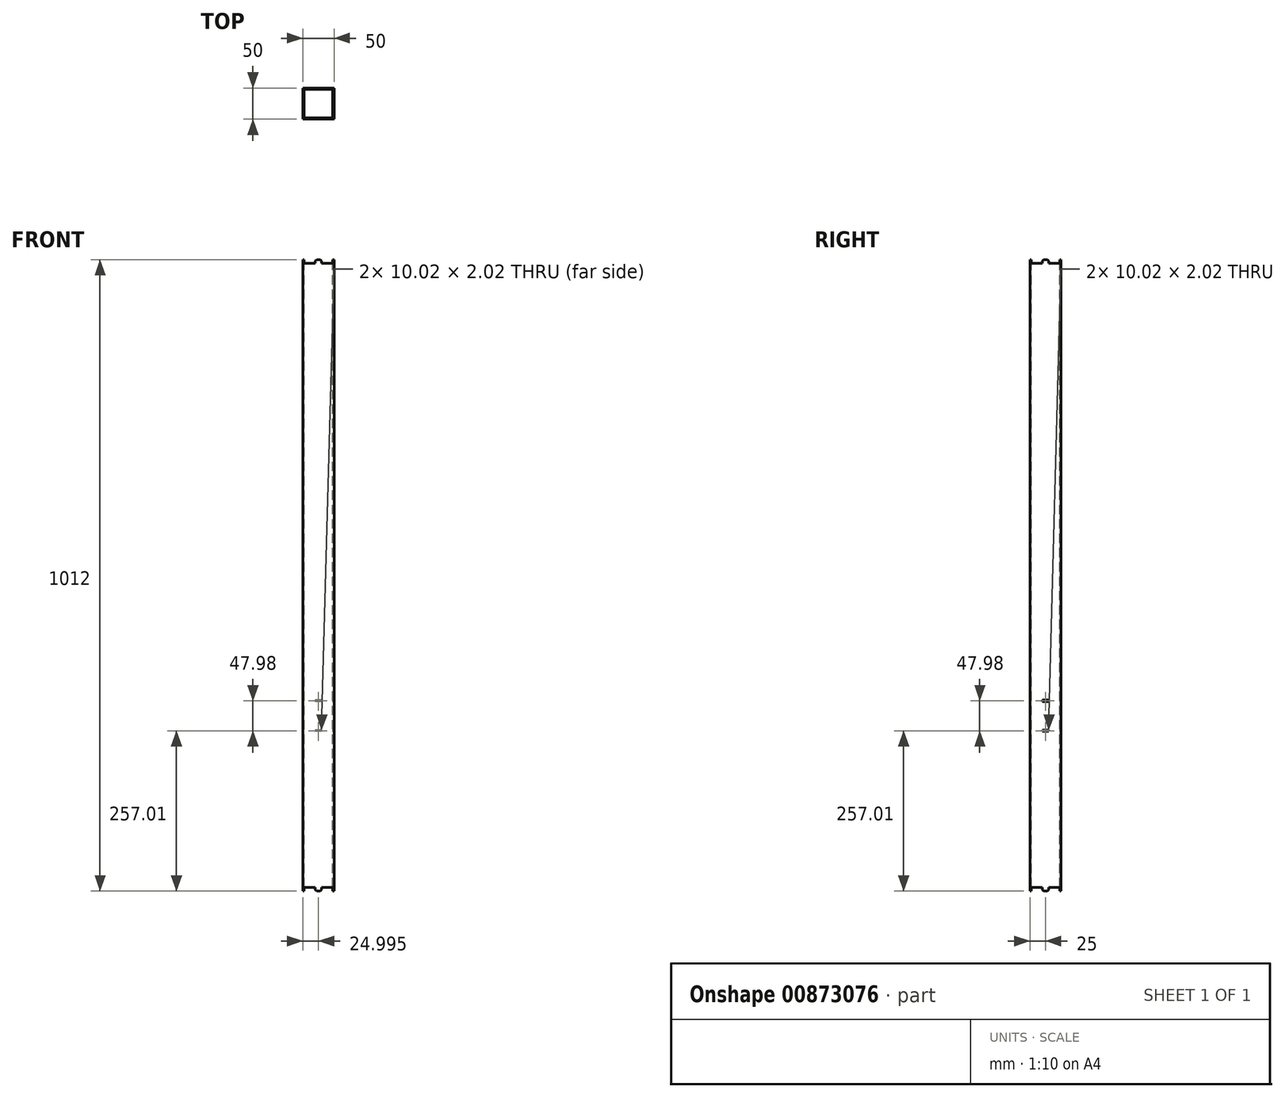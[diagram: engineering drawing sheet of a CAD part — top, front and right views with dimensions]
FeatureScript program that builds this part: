
annotation { "Feature Type Name" : "Feature", "Feature Type Description" : "" }
export const myFeature = defineFeature(function(context is Context, id is Id, definition is map)
    precondition{}
    {
        {
            var Q0;
            Q0=qCreatedBy(makeId("Front.planeOp"),FACE);
            var sketch = newSketch(context, id + "F0", { "sketchPlane" : qUnion([Q0])});
            skLineSegment(sketch, "E0.bottom", {"start": v(-56.86, 862.27) * mm, "end": v(-36.86, 862.27) * mm});
            skLineSegment(sketch, "E0.top", {"start": v(-56.86, -137.73) * mm, "end": v(-36.86, -137.73) * mm});
            skLineSegment(sketch, "E0.left", {"start": v(-56.86, 862.27) * mm, "end": v(-56.86, -137.73) * mm});
            skLineSegment(sketch, "E0.right", {"start": v(-6.86, 862.27) * mm, "end": v(-6.86, -137.73) * mm});
            skLineSegment(sketch, "E1", {"start": v(-36.86, -137.73) * mm, "end": v(-36.86, -141.73) * mm});
            skLineSegment(sketch, "E2", {"start": v(-36.86, -141.73) * mm, "end": v(-34.86, -143.73) * mm});
            skLineSegment(sketch, "E3", {"start": v(-34.86, -143.73) * mm, "end": v(-28.86, -143.73) * mm});
            skLineSegment(sketch, "E4", {"start": v(-28.86, -143.73) * mm, "end": v(-26.86, -141.73) * mm});
            skLineSegment(sketch, "E5", {"start": v(-26.86, -141.73) * mm, "end": v(-26.86, -137.73) * mm});
            skLineSegment(sketch, "E6.trimOffspring", {"start": v(-26.86, -137.73) * mm, "end": v(-6.86, -137.73) * mm});
            skLineSegment(sketch, "E7", {"start": v(-36.86, 862.27) * mm, "end": v(-36.86, 866.27) * mm});
            skLineSegment(sketch, "E8", {"start": v(-36.86, 866.27) * mm, "end": v(-34.86, 868.27) * mm});
            skLineSegment(sketch, "E9", {"start": v(-34.86, 868.27) * mm, "end": v(-28.86, 868.27) * mm});
            skLineSegment(sketch, "E10", {"start": v(-28.86, 868.27) * mm, "end": v(-26.86, 866.27) * mm});
            skLineSegment(sketch, "E11", {"start": v(-26.86, 866.27) * mm, "end": v(-26.86, 862.27) * mm});
            skLineSegment(sketch, "E12.trimOffspring", {"start": v(-26.86, 862.27) * mm, "end": v(-6.86, 862.27) * mm});
            skSolve(sketch);
        }
        {
            var Q0;
            Q0 = qSketchRegion(id + "F0", true);
            extrude(context, id + "F1", {"entities" : qUnion([Q0]), "depth" : 50 * mm, "offsetDistance" : 25 * mm});
        }
        {
            var Q0;
            Q0=makeQuery(id+"F1.opExtrude","SWEPT_FACE",FACE,{"disambiguationData":[OSD([sQuery(id+"F0.wireOp",EDGE,"E9")])]});
            var sketch = newSketch(context, id + "F2", { "sketchPlane" : qUnion([Q0])});
            skLineSegment(sketch, "E13.bottom", {"start": v(-54.86, -2) * mm, "end": v(-8.86, -2) * mm});
            skLineSegment(sketch, "E13.top", {"start": v(-54.86, -48) * mm, "end": v(-8.86, -48) * mm});
            skLineSegment(sketch, "E13.left", {"start": v(-54.86, -2) * mm, "end": v(-54.86, -48) * mm});
            skLineSegment(sketch, "E13.right", {"start": v(-8.86, -2) * mm, "end": v(-8.86, -48) * mm});
            skSolve(sketch);
        }
        {
            var Q0;
            Q0=makeQuery(id+"F1.opExtrude","SWEPT_FACE",FACE,{"disambiguationData":[OSD([sQuery(id+"F0.wireOp",EDGE,"E0.right")])]});
            var sketch = newSketch(context, id + "F3", { "sketchPlane" : qUnion([Q0])});
            skLineSegment(sketch, "E14", {"start": v(-30, 862.27) * mm, "end": v(-30, 866.27) * mm});
            skLineSegment(sketch, "E15", {"start": v(-30, 866.27) * mm, "end": v(-28, 868.27) * mm});
            skLineSegment(sketch, "E16", {"start": v(-28, 868.27) * mm, "end": v(-22, 868.27) * mm});
            skLineSegment(sketch, "E17", {"start": v(-22, 868.27) * mm, "end": v(-20, 866.27) * mm});
            skLineSegment(sketch, "E18", {"start": v(-20, 866.27) * mm, "end": v(-20, 862.27) * mm});
            skSolve(sketch);
        }
        {
            var Q0;
            Q0 = qSketchRegion(id + "F2", true);
            extrude(context, id + "F4", {"entities" : qUnion([Q0]), "operationType" : NewBodyOperationType.REMOVE, "endBound" : BoundingType.THROUGH_ALL, "oppositeDirection" : true, "depth" : 25 * mm, "offsetDistance" : 25 * mm});
        }
        {
            var Q0;
            Q0 = qSketchRegion(id + "F3", true);
            var Q1;
            {var subQ0=sQuery(id+"F3.wireOp",EDGE,"E14");Q1=makeQuery(id+"F3.imprint","IMPRINT",FACE,{"disambiguationData":[TD([[makeQuery(id+"F3.imprint","IMPRINT",EDGE,{"derivedFrom":subQ0}),-1.0]])]});}
            extrude(context, id + "F5", {"entities" : qUnion([Q0, Q1]), "operationType" : NewBodyOperationType.ADD, "oppositeDirection" : true, "depth" : 2 * mm, "offsetDistance" : 25 * mm});
        }
        {
            var Q0;
            Q0=makeQuery(id+"F1.opExtrude","SWEPT_FACE",FACE,{"disambiguationData":[OSD([sQuery(id+"F0.wireOp",EDGE,"E0.left")])]});
            var sketch = newSketch(context, id + "F6", { "sketchPlane" : qUnion([Q0])});
            skLineSegment(sketch, "E19", {"start": v(20, 862.27) * mm, "end": v(20, 866.27) * mm});
            skLineSegment(sketch, "E20", {"start": v(20, 866.27) * mm, "end": v(22, 868.27) * mm});
            skLineSegment(sketch, "E21", {"start": v(22, 868.27) * mm, "end": v(28, 868.27) * mm});
            skLineSegment(sketch, "E22", {"start": v(28, 868.27) * mm, "end": v(30, 866.27) * mm});
            skLineSegment(sketch, "E23", {"start": v(30, 866.27) * mm, "end": v(30, 862.27) * mm});
            skSolve(sketch);
        }
        {
            var Q0;
            Q0 = qSketchRegion(id + "F6", true);
            var Q1;
            {var subQ0=sQuery(id+"F6.wireOp",EDGE,"E19");Q1=makeQuery(id+"F6.imprint","IMPRINT",FACE,{"disambiguationData":[TD([[makeQuery(id+"F6.imprint","IMPRINT",EDGE,{"derivedFrom":subQ0}),-1.0]])]});}
            extrude(context, id + "F7", {"entities" : qUnion([Q0, Q1]), "operationType" : NewBodyOperationType.ADD, "oppositeDirection" : true, "depth" : 2 * mm, "offsetDistance" : 25 * mm});
        }
        {
            var Q0;
            {var subQ0=sQuery(id+"F0.wireOp",EDGE,"E0.left");Q0=makeQuery(id+"F7.boolean.opBoolean","MERGE",FACE,{"derivedFrom":[makeQuery(id+"F1.opExtrude","SWEPT_FACE",FACE,{"disambiguationData":[OSD([subQ0])]}),makeQuery(id+"F7.opExtrude","CAP_FACE",FACE,{"disambiguationData":[OSD([sQuery(id+"F0.wireOp",EDGE,"E0.bottom"),subQ0,sQuery(id+"F6.wireOp",EDGE,"E19"),sQuery(id+"F6.wireOp",EDGE,"E20"),sQuery(id+"F6.wireOp",EDGE,"E21"),sQuery(id+"F6.wireOp",EDGE,"E22"),sQuery(id+"F6.wireOp",EDGE,"E23")])],"isStart":true})]});}
            var sketch = newSketch(context, id + "F8", { "sketchPlane" : qUnion([Q0])});
            skLineSegment(sketch, "E24", {"start": v(20, -137.73) * mm, "end": v(20, -141.73) * mm});
            skLineSegment(sketch, "E25", {"start": v(20, -141.73) * mm, "end": v(21.68, -143.73) * mm});
            skLineSegment(sketch, "E26", {"start": v(21.68, -143.73) * mm, "end": v(28.32, -143.73) * mm});
            skLineSegment(sketch, "E27", {"start": v(28.32, -143.73) * mm, "end": v(30, -141.73) * mm});
            skLineSegment(sketch, "E28", {"start": v(30, -141.73) * mm, "end": v(30, -137.73) * mm});
            skSolve(sketch);
        }
        {
            var Q0;
            Q0 = qSketchRegion(id + "F8", true);
            var Q1;
            {var subQ0=sQuery(id+"F8.wireOp",EDGE,"E24");Q1=makeQuery(id+"F8.imprint","IMPRINT",FACE,{"disambiguationData":[TD([[makeQuery(id+"F8.imprint","IMPRINT",EDGE,{"derivedFrom":subQ0}),1.0]])]});}
            extrude(context, id + "F9", {"entities" : qUnion([Q0, Q1]), "operationType" : NewBodyOperationType.ADD, "oppositeDirection" : true, "depth" : 2 * mm, "offsetDistance" : 25 * mm});
        }
        {
            var Q0;
            {var subQ0=sQuery(id+"F0.wireOp",EDGE,"E0.right");Q0=makeQuery(id+"F5.boolean.opBoolean","MERGE",FACE,{"derivedFrom":[makeQuery(id+"F1.opExtrude","SWEPT_FACE",FACE,{"disambiguationData":[OSD([subQ0])]}),makeQuery(id+"F5.opExtrude","CAP_FACE",FACE,{"disambiguationData":[OSD([subQ0,sQuery(id+"F0.wireOp",EDGE,"E12.trimOffspring"),sQuery(id+"F3.wireOp",EDGE,"E14"),sQuery(id+"F3.wireOp",EDGE,"E15"),sQuery(id+"F3.wireOp",EDGE,"E16"),sQuery(id+"F3.wireOp",EDGE,"E17"),sQuery(id+"F3.wireOp",EDGE,"E18")])],"isStart":true})]});}
            var sketch = newSketch(context, id + "F10", { "sketchPlane" : qUnion([Q0])});
            skLineSegment(sketch, "E29", {"start": v(-30, -137.73) * mm, "end": v(-30, -141.73) * mm});
            skLineSegment(sketch, "E30", {"start": v(-30, -141.73) * mm, "end": v(-28, -143.73) * mm});
            skLineSegment(sketch, "E31", {"start": v(-28, -143.73) * mm, "end": v(-22, -143.73) * mm});
            skLineSegment(sketch, "E32", {"start": v(-22, -143.73) * mm, "end": v(-20, -141.73) * mm});
            skLineSegment(sketch, "E33", {"start": v(-20, -141.73) * mm, "end": v(-20, -137.73) * mm});
            skSolve(sketch);
        }
        {
            var Q0;
            Q0 = qSketchRegion(id + "F10", true);
            var Q1;
            {var subQ0=sQuery(id+"F10.wireOp",EDGE,"E29");Q1=makeQuery(id+"F10.imprint","IMPRINT",FACE,{"disambiguationData":[TD([[makeQuery(id+"F10.imprint","IMPRINT",EDGE,{"derivedFrom":subQ0}),1.0]])]});}
            extrude(context, id + "F11", {"entities" : qUnion([Q0, Q1]), "operationType" : NewBodyOperationType.ADD, "oppositeDirection" : true, "depth" : 2 * mm, "offsetDistance" : 25 * mm});
        }
        {
            var Q0;
            {var subQ0=sQuery(id+"F0.wireOp",EDGE,"E0.right");Q0=makeQuery(id+"F11.boolean.opBoolean","MERGE",FACE,{"derivedFrom":[makeQuery(id+"F5.boolean.opBoolean","MERGE",FACE,{"derivedFrom":[makeQuery(id+"F1.opExtrude","SWEPT_FACE",FACE,{"disambiguationData":[OSD([subQ0])]}),makeQuery(id+"F5.opExtrude","CAP_FACE",FACE,{"disambiguationData":[OSD([subQ0,sQuery(id+"F0.wireOp",EDGE,"E12.trimOffspring"),sQuery(id+"F3.wireOp",EDGE,"E14"),sQuery(id+"F3.wireOp",EDGE,"E15"),sQuery(id+"F3.wireOp",EDGE,"E16"),sQuery(id+"F3.wireOp",EDGE,"E17"),sQuery(id+"F3.wireOp",EDGE,"E18")])],"isStart":true})]}),makeQuery(id+"F11.opExtrude","CAP_FACE",FACE,{"disambiguationData":[OSD([subQ0,sQuery(id+"F0.wireOp",EDGE,"E6.trimOffspring"),sQuery(id+"F10.wireOp",EDGE,"E29"),sQuery(id+"F10.wireOp",EDGE,"E30"),sQuery(id+"F10.wireOp",EDGE,"E31"),sQuery(id+"F10.wireOp",EDGE,"E32"),sQuery(id+"F10.wireOp",EDGE,"E33")])],"isStart":true})]});}
            var sketch = newSketch(context, id + "F12", { "sketchPlane" : qUnion([Q0])});
            skLineSegment(sketch, "E34.bottom", {"start": v(-30.01, 162.27) * mm, "end": v(-19.99, 162.27) * mm});
            skLineSegment(sketch, "E34.top", {"start": v(-30.01, 160.25) * mm, "end": v(-19.99, 160.25) * mm});
            skLineSegment(sketch, "E34.left", {"start": v(-30.01, 162.27) * mm, "end": v(-30.01, 160.25) * mm});
            skLineSegment(sketch, "E34.right", {"start": v(-19.99, 162.27) * mm, "end": v(-19.99, 160.25) * mm});
            skLineSegment(sketch, "E35.bottom", {"start": v(-19.99, 114.29) * mm, "end": v(-30.01, 114.29) * mm});
            skLineSegment(sketch, "E35.top", {"start": v(-20, 112.27) * mm, "end": v(-30.01, 112.27) * mm});
            skLineSegment(sketch, "E35.left", {"start": v(-20, 114.29) * mm, "end": v(-20, 112.27) * mm});
            skLineSegment(sketch, "E35.right", {"start": v(-30.01, 114.29) * mm, "end": v(-30.01, 112.27) * mm});
            skSolve(sketch);
        }
        {
            var Q0;
            Q0=makeQuery(id+"F12.imprint","IMPRINT",FACE,{"disambiguationData":[TD([[makeQuery(id+"F12.imprint","IMPRINT",EDGE,{"derivedFrom":sQuery(id+"F12.wireOp",EDGE,"E34.bottom")}),-1.0]])]});
            var Q1;
            Q1=makeQuery(id+"F12.imprint","IMPRINT",FACE,{"disambiguationData":[TD([[makeQuery(id+"F12.imprint","IMPRINT",EDGE,{"derivedFrom":sQuery(id+"F12.wireOp",EDGE,"E35.bottom")}),1.0]])]});
            extrude(context, id + "F13", {"entities" : qUnion([Q0, Q1]), "operationType" : NewBodyOperationType.REMOVE, "oppositeDirection" : true, "depth" : 2 * mm, "offsetDistance" : 25 * mm});
        }
        {
            var Q0;
            Q0=makeQuery(id+"F1.opExtrude","CAP_FACE",FACE,{"disambiguationData":[OSD([sQuery(id+"F0.wireOp",EDGE,"E0.bottom"),sQuery(id+"F0.wireOp",EDGE,"E0.top"),sQuery(id+"F0.wireOp",EDGE,"E0.left"),sQuery(id+"F0.wireOp",EDGE,"E0.right"),sQuery(id+"F0.wireOp",EDGE,"E1"),sQuery(id+"F0.wireOp",EDGE,"E2"),sQuery(id+"F0.wireOp",EDGE,"E3"),sQuery(id+"F0.wireOp",EDGE,"E4"),sQuery(id+"F0.wireOp",EDGE,"E5"),sQuery(id+"F0.wireOp",EDGE,"E6.trimOffspring"),sQuery(id+"F0.wireOp",EDGE,"E7"),sQuery(id+"F0.wireOp",EDGE,"E8"),sQuery(id+"F0.wireOp",EDGE,"E9"),sQuery(id+"F0.wireOp",EDGE,"E10"),sQuery(id+"F0.wireOp",EDGE,"E11"),sQuery(id+"F0.wireOp",EDGE,"E12.trimOffspring")])],"isStart":true});
            var sketch = newSketch(context, id + "F14", { "sketchPlane" : qUnion([Q0])});
            skLineSegment(sketch, "E36.bottom", {"start": v(26.85, 162.27) * mm, "end": v(36.87, 162.27) * mm});
            skLineSegment(sketch, "E36.top", {"start": v(26.85, 160.25) * mm, "end": v(36.87, 160.25) * mm});
            skLineSegment(sketch, "E36.left", {"start": v(26.85, 162.27) * mm, "end": v(26.85, 160.25) * mm});
            skLineSegment(sketch, "E36.right", {"start": v(36.87, 162.27) * mm, "end": v(36.87, 160.25) * mm});
            skLineSegment(sketch, "E37.bottom", {"start": v(26.85, 114.29) * mm, "end": v(36.87, 114.29) * mm});
            skLineSegment(sketch, "E37.top", {"start": v(26.85, 112.27) * mm, "end": v(36.87, 112.27) * mm});
            skLineSegment(sketch, "E37.left", {"start": v(26.85, 114.29) * mm, "end": v(26.85, 112.27) * mm});
            skLineSegment(sketch, "E37.right", {"start": v(36.87, 114.29) * mm, "end": v(36.87, 112.27) * mm});
            skSolve(sketch);
        }
        {
            var Q0;
            Q0=makeQuery(id+"F14.imprint","IMPRINT",FACE,{"disambiguationData":[TD([[makeQuery(id+"F14.imprint","IMPRINT",EDGE,{"derivedFrom":sQuery(id+"F14.wireOp",EDGE,"E36.bottom")}),-1.0]])]});
            var Q1;
            Q1=makeQuery(id+"F14.imprint","IMPRINT",FACE,{"disambiguationData":[TD([[makeQuery(id+"F14.imprint","IMPRINT",EDGE,{"derivedFrom":sQuery(id+"F14.wireOp",EDGE,"E37.bottom")}),-1.0]])]});
            extrude(context, id + "F15", {"entities" : qUnion([Q0, Q1]), "operationType" : NewBodyOperationType.REMOVE, "oppositeDirection" : true, "depth" : 2 * mm, "offsetDistance" : 25 * mm});
        }
    });
